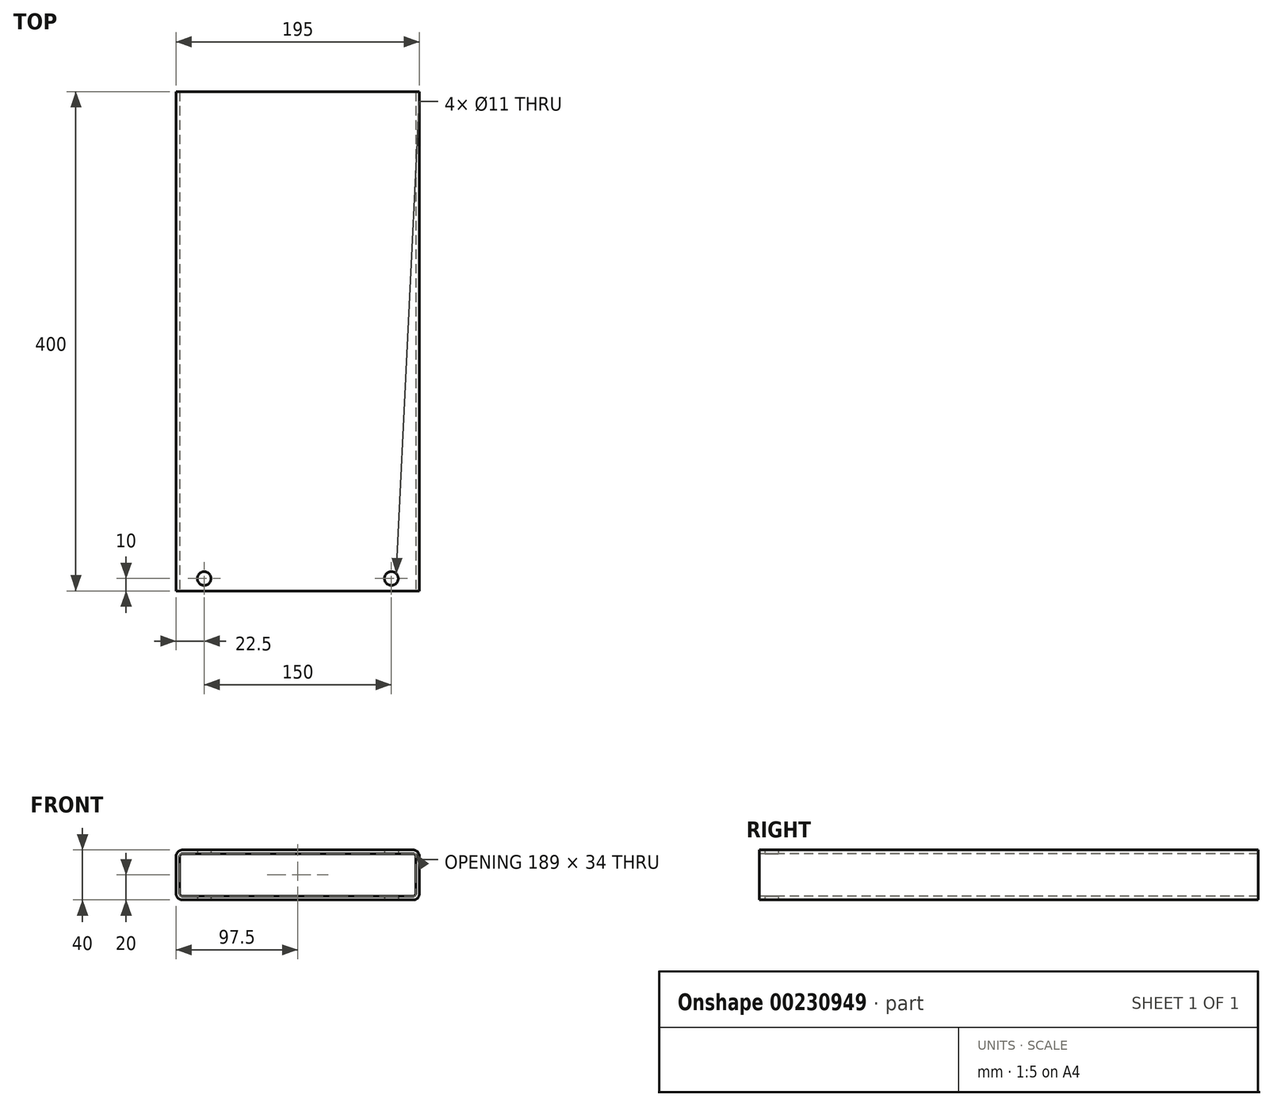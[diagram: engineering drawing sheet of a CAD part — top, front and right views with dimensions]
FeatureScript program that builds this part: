
annotation { "Feature Type Name" : "Feature", "Feature Type Description" : "" }
export const myFeature = defineFeature(function(context is Context, id is Id, definition is map)
    precondition{}
    {
        {
            var Q0;
            Q0=qCreatedBy(makeId("Front.planeOp"),FACE);
            var sketch = newSketch(context, id + "F0", { "sketchPlane" : qUnion([Q0])});
            skLineSegment(sketch, "E0", {"start": v(0, -45.42) * mm, "end": v(0, 57.63) * mm, "construction": true});
            skLineSegment(sketch, "E1.bottom", {"start": v(-92.5, 0) * mm, "end": v(92.5, 0) * mm});
            skLineSegment(sketch, "E1.top", {"start": v(-92.5, 40) * mm, "end": v(92.5, 40) * mm});
            skLineSegment(sketch, "E1.left", {"start": v(-97.5, 5) * mm, "end": v(-97.5, 35) * mm});
            skLineSegment(sketch, "E1.right", {"start": v(97.5, 5) * mm, "end": v(97.5, 35) * mm});
            skLineSegment(sketch, "E2.0", {"start": v(-92.5, 37) * mm, "end": v(92.5, 37) * mm});
            skLineSegment(sketch, "E2.1", {"start": v(-94.5, 5) * mm, "end": v(-94.5, 35) * mm});
            skLineSegment(sketch, "E2.2", {"start": v(-92.5, 3) * mm, "end": v(92.5, 3) * mm});
            skLineSegment(sketch, "E2.3", {"start": v(94.5, 5) * mm, "end": v(94.5, 35) * mm});
            skPoint(sketch, "E3.visualSharp", {"position": v(-94.5, 37) * mm});
            skArc(sketch, "E3.filletArc", {"start": v(-92.5, 37) * mm, "mid": v(-93.91, 36.41) * mm, "end": v(-94.5, 35) * mm});
            skPoint(sketch, "E4.visualSharp", {"position": v(-94.5, 3) * mm});
            skArc(sketch, "E4.filletArc", {"start": v(-94.5, 5) * mm, "mid": v(-93.91, 3.59) * mm, "end": v(-92.5, 3) * mm});
            skPoint(sketch, "E5.visualSharp", {"position": v(94.5, 3) * mm});
            skArc(sketch, "E5.filletArc", {"start": v(92.5, 3) * mm, "mid": v(93.91, 3.59) * mm, "end": v(94.5, 5) * mm});
            skPoint(sketch, "E6.visualSharp", {"position": v(94.5, 37) * mm});
            skArc(sketch, "E6.filletArc", {"start": v(94.5, 35) * mm, "mid": v(93.91, 36.41) * mm, "end": v(92.5, 37) * mm});
            skPoint(sketch, "E7.visualSharp", {"position": v(97.5, 40) * mm});
            skArc(sketch, "E7.filletArc", {"start": v(97.5, 35) * mm, "mid": v(96.04, 38.54) * mm, "end": v(92.5, 40) * mm});
            skPoint(sketch, "E8.visualSharp", {"position": v(97.5, 0) * mm});
            skArc(sketch, "E8.filletArc", {"start": v(92.5, 0) * mm, "mid": v(96.04, 1.46) * mm, "end": v(97.5, 5) * mm});
            skPoint(sketch, "E9.visualSharp", {"position": v(-97.5, 0) * mm});
            skArc(sketch, "E9.filletArc", {"start": v(-97.5, 5) * mm, "mid": v(-96.04, 1.46) * mm, "end": v(-92.5, 0) * mm});
            skPoint(sketch, "E10.visualSharp", {"position": v(-97.5, 40) * mm});
            skArc(sketch, "E10.filletArc", {"start": v(-92.5, 40) * mm, "mid": v(-96.04, 38.54) * mm, "end": v(-97.5, 35) * mm});
            skSolve(sketch);
        }
        {
            var Q0;
            Q0 = qSketchRegion(id + "F0", true);
            extrude(context, id + "F1", {"entities" : qUnion([Q0]), "oppositeDirection" : true, "depth" : 400 * mm});
        }
        {
            var Q0;
            Q0=makeQuery(id+"F1.opExtrude","SWEPT_FACE",FACE,{"disambiguationData":[OSD([sQuery(id+"F0.wireOp",EDGE,"E1.top")])]});
            var sketch = newSketch(context, id + "F2", { "sketchPlane" : qUnion([Q0])});
            skCircle(sketch, "E11", {"center": v(-75, 10) * mm, "radius": 5 * mm});
            skCircle(sketch, "E12", {"center": v(75, 10) * mm, "radius": 5 * mm});
            skSolve(sketch);
        }
        {
            var Q0;
            Q0=sQuery(id+"F2.wireOp",VERTEX,"E11.center");
            var Q1;
            Q1=sQuery(id+"F2.wireOp",VERTEX,"E12.center");
            var Q2;
            Q2=makeQuery(id+"F1.opExtrude","SWEPT_BODY",BODY,{"disambiguationData":[OSD([sQuery(id+"F0.wireOp",EDGE,"E1.bottom"),sQuery(id+"F0.wireOp",EDGE,"E1.top"),sQuery(id+"F0.wireOp",EDGE,"E1.left"),sQuery(id+"F0.wireOp",EDGE,"E1.right"),sQuery(id+"F0.wireOp",EDGE,"E2.0"),sQuery(id+"F0.wireOp",EDGE,"E2.1"),sQuery(id+"F0.wireOp",EDGE,"E2.2"),sQuery(id+"F0.wireOp",EDGE,"E2.3"),sQuery(id+"F0.wireOp",EDGE,"E3.filletArc"),sQuery(id+"F0.wireOp",EDGE,"E4.filletArc"),sQuery(id+"F0.wireOp",EDGE,"E5.filletArc"),sQuery(id+"F0.wireOp",EDGE,"E6.filletArc"),sQuery(id+"F0.wireOp",EDGE,"E7.filletArc"),sQuery(id+"F0.wireOp",EDGE,"E8.filletArc"),sQuery(id+"F0.wireOp",EDGE,"E9.filletArc"),sQuery(id+"F0.wireOp",EDGE,"E10.filletArc")])]});
            hole(context, id + "F3", {"style" : HoleStyle.SIMPLE, "endStyle" : HoleEndStyle.THROUGH, "standardTappedOrClearance" : lookupTablePath({ "standard" : "ISO", "fit" : "Normal", "size" : "M10", "type" : "Clearance" }), "standardBlindInLast" : lookupTablePath({ "fit" : "Standard", "standard" : "ISO", "size" : "M10", "type" : "Clearance" }), "holeDiameter" : 11 * mm, "locations" : qUnion([Q0, Q1]), "scope" : qUnion([Q2]), "isTappedThrough" : true, "startStyle" : HoleStartStyle.SKETCH});
        }
    });
